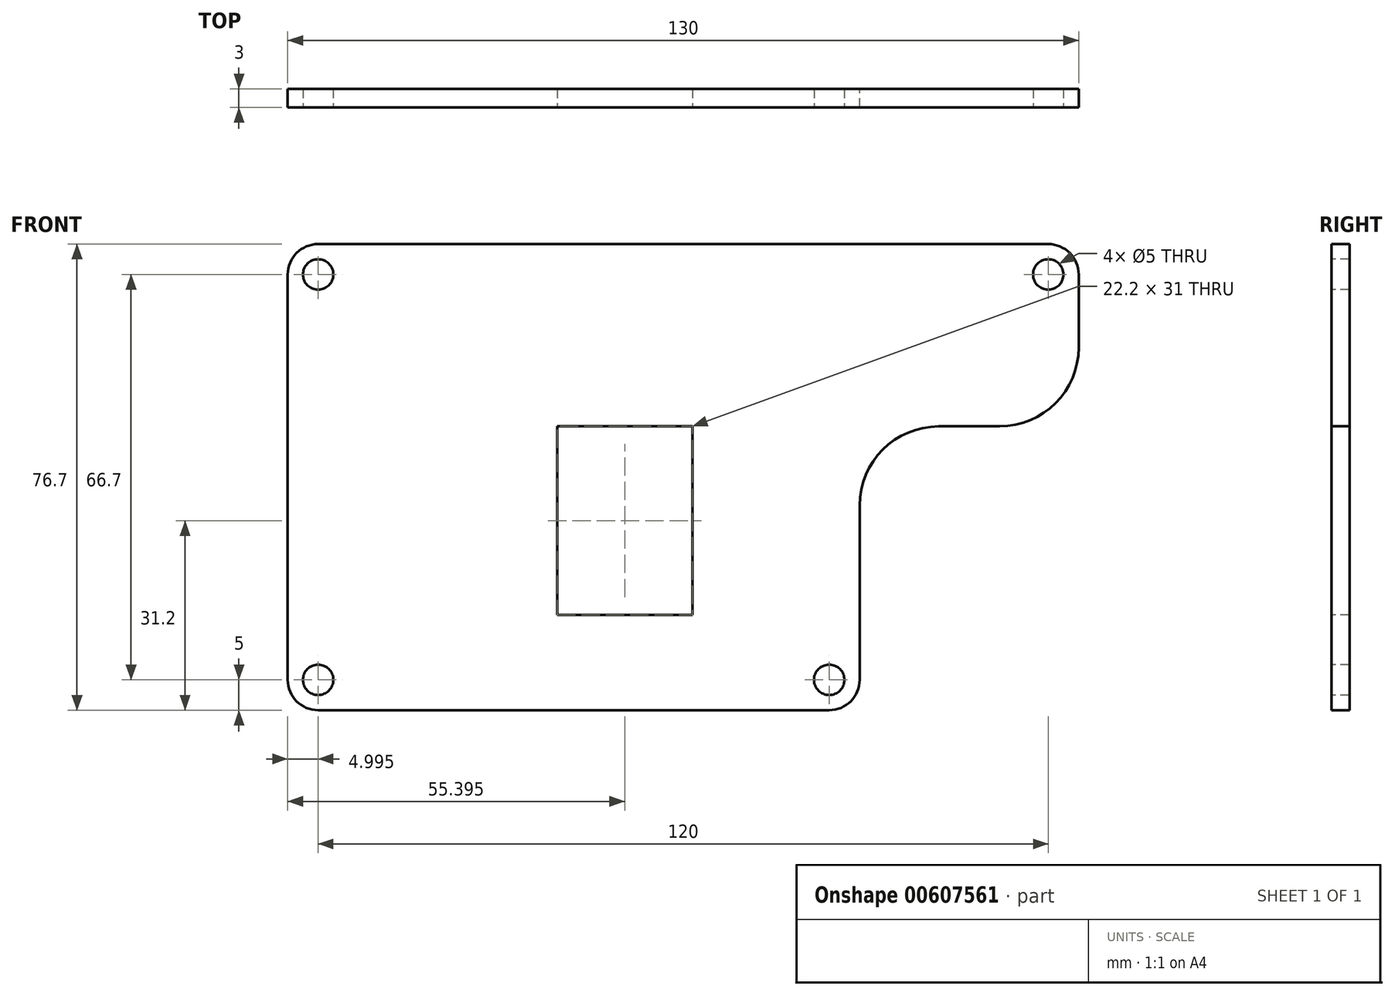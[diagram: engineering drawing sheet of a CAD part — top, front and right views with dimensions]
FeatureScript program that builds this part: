
annotation { "Feature Type Name" : "Feature", "Feature Type Description" : "" }
export const myFeature = defineFeature(function(context is Context, id is Id, definition is map)
    precondition{}
    {
        {
            var Q0;
            Q0=qCreatedBy(makeId("Front.planeOp"),FACE);
            var sketch = newSketch(context, id + "F0", { "sketchPlane" : qUnion([Q0])});
            skLineSegment(sketch, "E0", {"start": v(-57.13, 30) * mm, "end": v(72.87, 30) * mm});
            skLineSegment(sketch, "E1", {"start": v(72.87, 30) * mm, "end": v(72.87, 0) * mm});
            skLineSegment(sketch, "E2", {"start": v(72.87, 0) * mm, "end": v(36.87, 0) * mm});
            skLineSegment(sketch, "E3", {"start": v(36.87, 0) * mm, "end": v(36.87, -46.7) * mm});
            skLineSegment(sketch, "E4", {"start": v(36.87, -46.7) * mm, "end": v(-57.13, -46.7) * mm});
            skLineSegment(sketch, "E5", {"start": v(-57.13, -46.7) * mm, "end": v(-57.13, 30) * mm});
            skSolve(sketch);
        }
        {
            var Q0;
            Q0=makeQuery(id+"F0.imprint","IMPRINT",FACE,{"disambiguationData":[TD([[makeQuery(id+"F0.imprint","IMPRINT",EDGE,{"derivedFrom":sQuery(id+"F0.wireOp",EDGE,"E0")}),-1.0]])]});
            extrude(context, id + "F1", {"entities" : qUnion([Q0]), "depth" : 3 * mm, "offsetDistance" : 25 * mm});
        }
        {
            var Q0;
            Q0=makeQuery(id+"F1.opExtrude","CAP_FACE",FACE,{"disambiguationData":[OSD([sQuery(id+"F0.wireOp",EDGE,"E0"),sQuery(id+"F0.wireOp",EDGE,"E1"),sQuery(id+"F0.wireOp",EDGE,"E2"),sQuery(id+"F0.wireOp",EDGE,"E3"),sQuery(id+"F0.wireOp",EDGE,"E4"),sQuery(id+"F0.wireOp",EDGE,"E5")])],"isStart":false});
            var sketch = newSketch(context, id + "F2", { "sketchPlane" : qUnion([Q0])});
            skLineSegment(sketch, "E6.bottom", {"start": v(-12.83, 0) * mm, "end": v(9.37, 0) * mm});
            skLineSegment(sketch, "E6.top", {"start": v(-12.83, -31) * mm, "end": v(9.37, -31) * mm});
            skLineSegment(sketch, "E6.left", {"start": v(-12.83, 0) * mm, "end": v(-12.83, -31) * mm});
            skLineSegment(sketch, "E6.right", {"start": v(9.37, 0) * mm, "end": v(9.37, -31) * mm});
            skSolve(sketch);
        }
        {
            var Q0;
            Q0=makeQuery(id+"F2.imprint","IMPRINT",FACE,{"disambiguationData":[TD([[makeQuery(id+"F2.imprint","IMPRINT",EDGE,{"derivedFrom":sQuery(id+"F2.wireOp",EDGE,"E6.bottom")}),-1.0]])]});
            extrude(context, id + "F3", {"entities" : qUnion([Q0]), "operationType" : NewBodyOperationType.REMOVE, "oppositeDirection" : true, "depth" : 25 * mm, "offsetDistance" : 25 * mm});
        }
        {
            var Q0;
            Q0=makeQuery(id+"F1.opExtrude","SWEPT_EDGE",EDGE,{"disambiguationData":[OSD([sQuery(id+"F0.wireOp",EDGE,"E1"),sQuery(id+"F0.wireOp",EDGE,"E2")])]});
            fillet(context, id + "F4", {"entities" : qUnion([Q0]), "radius" : 13 * mm, "tangentPropagation" : true, "allowEdgeOverflow" : false});
        }
        {
            var Q0;
            Q0=makeQuery(id+"F1.opExtrude","SWEPT_EDGE",EDGE,{"disambiguationData":[OSD([sQuery(id+"F0.wireOp",EDGE,"E2"),sQuery(id+"F0.wireOp",EDGE,"E3")])]});
            fillet(context, id + "F5", {"entities" : qUnion([Q0]), "radius" : 13 * mm, "tangentPropagation" : true, "allowEdgeOverflow" : false});
        }
        {
            var Q0;
            Q0=makeQuery(id+"F1.opExtrude","SWEPT_EDGE",EDGE,{"disambiguationData":[OSD([sQuery(id+"F0.wireOp",EDGE,"E0"),sQuery(id+"F0.wireOp",EDGE,"E1")])]});
            fillet(context, id + "F6", {"entities" : qUnion([Q0]), "radius" : 5 * mm, "tangentPropagation" : true, "allowEdgeOverflow" : false});
        }
        {
            var Q0;
            Q0=makeQuery(id+"F1.opExtrude","SWEPT_EDGE",EDGE,{"disambiguationData":[OSD([sQuery(id+"F0.wireOp",EDGE,"E3"),sQuery(id+"F0.wireOp",EDGE,"E4")])]});
            fillet(context, id + "F7", {"entities" : qUnion([Q0]), "radius" : 5 * mm, "tangentPropagation" : true, "allowEdgeOverflow" : false});
        }
        {
            var Q0;
            Q0=makeQuery(id+"F1.opExtrude","SWEPT_EDGE",EDGE,{"disambiguationData":[OSD([sQuery(id+"F0.wireOp",EDGE,"E4"),sQuery(id+"F0.wireOp",EDGE,"E5")])]});
            fillet(context, id + "F8", {"entities" : qUnion([Q0]), "radius" : 5 * mm, "tangentPropagation" : true, "allowEdgeOverflow" : false});
        }
        {
            var Q0;
            Q0=makeQuery(id+"F1.opExtrude","SWEPT_EDGE",EDGE,{"disambiguationData":[OSD([sQuery(id+"F0.wireOp",EDGE,"E0"),sQuery(id+"F0.wireOp",EDGE,"E5")])]});
            fillet(context, id + "F9", {"entities" : qUnion([Q0]), "radius" : 5 * mm, "tangentPropagation" : true, "allowEdgeOverflow" : false});
        }
        {
            var Q0;
            Q0=makeQuery(id+"F1.opExtrude","CAP_FACE",FACE,{"disambiguationData":[OSD([sQuery(id+"F0.wireOp",EDGE,"E0"),sQuery(id+"F0.wireOp",EDGE,"E1"),sQuery(id+"F0.wireOp",EDGE,"E2"),sQuery(id+"F0.wireOp",EDGE,"E3"),sQuery(id+"F0.wireOp",EDGE,"E4"),sQuery(id+"F0.wireOp",EDGE,"E5")])],"isStart":false});
            var sketch = newSketch(context, id + "F10", { "sketchPlane" : qUnion([Q0])});
            skCircle(sketch, "E7", {"center": v(-52.13, 25) * mm, "radius": 2.5 * mm});
            skSolve(sketch);
        }
        {
            var Q0;
            Q0=makeQuery(id+"F10.imprint","IMPRINT",FACE,{"disambiguationData":[TD([[makeQuery(id+"F10.imprint","IMPRINT",EDGE,{"derivedFrom":sQuery(id+"F10.wireOp",EDGE,"E7")}),1.0]])]});
            extrude(context, id + "F11", {"entities" : qUnion([Q0]), "operationType" : NewBodyOperationType.REMOVE, "oppositeDirection" : true, "depth" : 25 * mm, "offsetDistance" : 25 * mm});
        }
        {
            var Q0;
            Q0=makeQuery(id+"F1.opExtrude","CAP_FACE",FACE,{"disambiguationData":[OSD([sQuery(id+"F0.wireOp",EDGE,"E0"),sQuery(id+"F0.wireOp",EDGE,"E1"),sQuery(id+"F0.wireOp",EDGE,"E2"),sQuery(id+"F0.wireOp",EDGE,"E3"),sQuery(id+"F0.wireOp",EDGE,"E4"),sQuery(id+"F0.wireOp",EDGE,"E5")])],"isStart":false});
            var sketch = newSketch(context, id + "F12", { "sketchPlane" : qUnion([Q0])});
            skCircle(sketch, "E8", {"center": v(67.87, 25) * mm, "radius": 2.5 * mm});
            skSolve(sketch);
        }
        {
            var Q0;
            Q0=makeQuery(id+"F12.imprint","IMPRINT",FACE,{"disambiguationData":[TD([[makeQuery(id+"F12.imprint","IMPRINT",EDGE,{"derivedFrom":sQuery(id+"F12.wireOp",EDGE,"E8")}),1.0]])]});
            extrude(context, id + "F13", {"entities" : qUnion([Q0]), "operationType" : NewBodyOperationType.REMOVE, "oppositeDirection" : true, "depth" : 25 * mm, "offsetDistance" : 25 * mm});
        }
        {
            var Q0;
            Q0=makeQuery(id+"F1.opExtrude","CAP_FACE",FACE,{"disambiguationData":[OSD([sQuery(id+"F0.wireOp",EDGE,"E0"),sQuery(id+"F0.wireOp",EDGE,"E1"),sQuery(id+"F0.wireOp",EDGE,"E2"),sQuery(id+"F0.wireOp",EDGE,"E3"),sQuery(id+"F0.wireOp",EDGE,"E4"),sQuery(id+"F0.wireOp",EDGE,"E5")])],"isStart":false});
            var sketch = newSketch(context, id + "F14", { "sketchPlane" : qUnion([Q0])});
            skCircle(sketch, "E9", {"center": v(-52.13, -41.7) * mm, "radius": 2.5 * mm});
            skSolve(sketch);
        }
        {
            var Q0;
            Q0=makeQuery(id+"F14.imprint","IMPRINT",FACE,{"disambiguationData":[TD([[makeQuery(id+"F14.imprint","IMPRINT",EDGE,{"derivedFrom":sQuery(id+"F14.wireOp",EDGE,"E9")}),1.0]])]});
            extrude(context, id + "F15", {"entities" : qUnion([Q0]), "operationType" : NewBodyOperationType.REMOVE, "oppositeDirection" : true, "depth" : 25 * mm, "offsetDistance" : 25 * mm});
        }
        {
            var Q0;
            Q0=makeQuery(id+"F1.opExtrude","CAP_FACE",FACE,{"disambiguationData":[OSD([sQuery(id+"F0.wireOp",EDGE,"E0"),sQuery(id+"F0.wireOp",EDGE,"E1"),sQuery(id+"F0.wireOp",EDGE,"E2"),sQuery(id+"F0.wireOp",EDGE,"E3"),sQuery(id+"F0.wireOp",EDGE,"E4"),sQuery(id+"F0.wireOp",EDGE,"E5")])],"isStart":false});
            var sketch = newSketch(context, id + "F16", { "sketchPlane" : qUnion([Q0])});
            skCircle(sketch, "E10", {"center": v(31.87, -41.7) * mm, "radius": 2.5 * mm});
            skSolve(sketch);
        }
        {
            var Q0;
            Q0=makeQuery(id+"F16.imprint","IMPRINT",FACE,{"disambiguationData":[TD([[makeQuery(id+"F16.imprint","IMPRINT",EDGE,{"derivedFrom":sQuery(id+"F16.wireOp",EDGE,"E10")}),1.0]])]});
            extrude(context, id + "F17", {"entities" : qUnion([Q0]), "operationType" : NewBodyOperationType.REMOVE, "oppositeDirection" : true, "depth" : 25 * mm, "offsetDistance" : 25 * mm});
        }
    });
